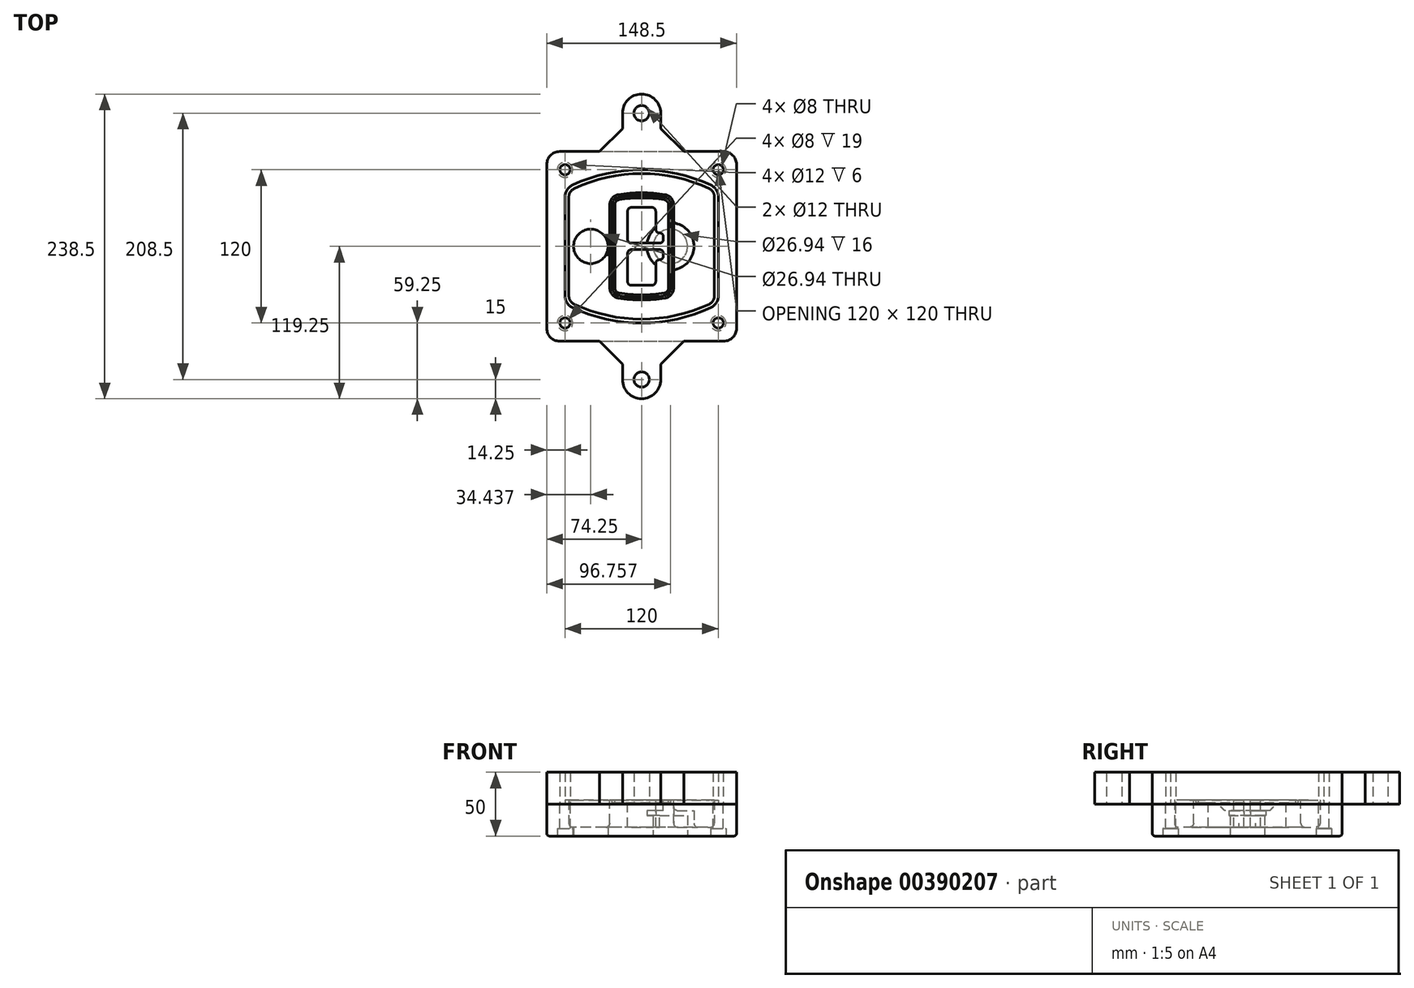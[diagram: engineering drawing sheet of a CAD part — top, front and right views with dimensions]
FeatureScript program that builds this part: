
annotation { "Feature Type Name" : "Feature", "Feature Type Description" : "" }
export const myFeature = defineFeature(function(context is Context, id is Id, definition is map)
    precondition{}
    {
        {
            var Q0;
            Q0=qCreatedBy(makeId("Top.planeOp"),FACE);
            var sketch = newSketch(context, id + "F0", { "sketchPlane" : qUnion([Q0])});
            skPoint(sketch, "E0.rect.middle", {"position": v(0, 0) * mm});
            skLineSegment(sketch, "E1.bottom", {"start": v(-64.25, -74.25) * mm, "end": v(64.25, -74.25) * mm});
            skLineSegment(sketch, "E1.top", {"start": v(-64.25, 74.25) * mm, "end": v(64.25, 74.25) * mm});
            skLineSegment(sketch, "E1.left", {"start": v(-74.25, -64.25) * mm, "end": v(-74.25, 64.25) * mm});
            skLineSegment(sketch, "E1.right", {"start": v(74.25, -64.25) * mm, "end": v(74.25, 64.25) * mm});
            skLineSegment(sketch, "E2", {"start": v(-74.25, 74.25) * mm, "end": v(74.25, -74.25) * mm, "construction": true});
            skLineSegment(sketch, "E3", {"start": v(74.25, 74.25) * mm, "end": v(-74.25, -74.25) * mm, "construction": true});
            skCircle(sketch, "E4", {"center": v(-60, 60) * mm, "radius": 4 * mm});
            skCircle(sketch, "E5", {"center": v(60, 60) * mm, "radius": 4 * mm});
            skCircle(sketch, "E6", {"center": v(60, -60) * mm, "radius": 4 * mm});
            skCircle(sketch, "E7", {"center": v(-60, -60) * mm, "radius": 4 * mm});
            skLineSegment(sketch, "E8", {"start": v(-60, 60) * mm, "end": v(60, 60) * mm, "construction": true});
            skLineSegment(sketch, "E9", {"start": v(60, 60) * mm, "end": v(60, -60) * mm, "construction": true});
            skLineSegment(sketch, "E10", {"start": v(60, -60) * mm, "end": v(-60, -60) * mm, "construction": true});
            skLineSegment(sketch, "E11", {"start": v(-60, -60) * mm, "end": v(-60, 60) * mm, "construction": true});
            skLineSegment(sketch, "E12", {"start": v(-60, 38.83) * mm, "end": v(-60, -38.83) * mm});
            skLineSegment(sketch, "E13", {"start": v(60, 38.83) * mm, "end": v(60, -38.83) * mm});
            skArc(sketch, "E14", {"start": v(54.26, 47.88) * mm, "mid": v(0, 60) * mm, "end": v(-54.26, 47.88) * mm});
            skArc(sketch, "E15", {"start": v(-54.26, -47.88) * mm, "mid": v(0, -60) * mm, "end": v(54.26, -47.88) * mm});
            skLineSegment(sketch, "E16", {"start": v(-60, 0) * mm, "end": v(60, 0) * mm, "construction": true});
            skPoint(sketch, "E17.visualSharp", {"position": v(-60, -45) * mm});
            skArc(sketch, "E17.filletArc", {"start": v(-60, -38.83) * mm, "mid": v(-58.44, -44.2) * mm, "end": v(-54.26, -47.88) * mm});
            skPoint(sketch, "E18.visualSharp", {"position": v(-60, 45) * mm});
            skArc(sketch, "E18.filletArc", {"start": v(-54.26, 47.88) * mm, "mid": v(-58.44, 44.2) * mm, "end": v(-60, 38.83) * mm});
            skPoint(sketch, "E19.visualSharp", {"position": v(60, 45) * mm});
            skArc(sketch, "E19.filletArc", {"start": v(60, 38.83) * mm, "mid": v(58.44, 44.2) * mm, "end": v(54.26, 47.88) * mm});
            skPoint(sketch, "E20.visualSharp", {"position": v(60, -45) * mm});
            skArc(sketch, "E20.filletArc", {"start": v(54.26, -47.88) * mm, "mid": v(58.44, -44.2) * mm, "end": v(60, -38.83) * mm});
            skPoint(sketch, "E21.visualSharp", {"position": v(-74.25, 74.25) * mm});
            skArc(sketch, "E21.filletArc", {"start": v(-64.25, 74.25) * mm, "mid": v(-71.32, 71.32) * mm, "end": v(-74.25, 64.25) * mm});
            skPoint(sketch, "E22.visualSharp", {"position": v(74.25, 74.25) * mm});
            skArc(sketch, "E22.filletArc", {"start": v(74.25, 64.25) * mm, "mid": v(71.32, 71.32) * mm, "end": v(64.25, 74.25) * mm});
            skPoint(sketch, "E23.visualSharp", {"position": v(74.25, -74.25) * mm});
            skArc(sketch, "E23.filletArc", {"start": v(64.25, -74.25) * mm, "mid": v(71.32, -71.32) * mm, "end": v(74.25, -64.25) * mm});
            skPoint(sketch, "E24.visualSharp", {"position": v(-74.25, -74.25) * mm});
            skArc(sketch, "E24.filletArc", {"start": v(-74.25, -64.25) * mm, "mid": v(-71.32, -71.32) * mm, "end": v(-64.25, -74.25) * mm});
            skArc(sketch, "E25.0", {"start": v(57, 38.83) * mm, "mid": v(55.9, 42.58) * mm, "end": v(52.98, 45.17) * mm});
            skLineSegment(sketch, "E25.1", {"start": v(57, 38.83) * mm, "end": v(57, -38.83) * mm});
            skArc(sketch, "E25.2", {"start": v(52.98, -45.17) * mm, "mid": v(55.9, -42.58) * mm, "end": v(57, -38.83) * mm});
            skArc(sketch, "E25.3", {"start": v(-52.98, -45.17) * mm, "mid": v(0, -57) * mm, "end": v(52.98, -45.17) * mm});
            skArc(sketch, "E25.4", {"start": v(-57, -38.83) * mm, "mid": v(-55.9, -42.58) * mm, "end": v(-52.98, -45.17) * mm});
            skArc(sketch, "E25.5", {"start": v(52.98, 45.17) * mm, "mid": v(0, 57) * mm, "end": v(-52.98, 45.17) * mm});
            skLineSegment(sketch, "E25.6", {"start": v(-57, 38.83) * mm, "end": v(-57, -38.83) * mm});
            skArc(sketch, "E25.7", {"start": v(-52.98, 45.17) * mm, "mid": v(-55.9, 42.58) * mm, "end": v(-57, 38.83) * mm});
            skArc(sketch, "E26.0", {"start": v(-55.96, 51.5) * mm, "mid": v(-61.82, 46.33) * mm, "end": v(-64, 38.83) * mm});
            skArc(sketch, "E26.1", {"start": v(55.96, 51.5) * mm, "mid": v(0, 64) * mm, "end": v(-55.96, 51.5) * mm});
            skArc(sketch, "E26.2", {"start": v(64, 38.83) * mm, "mid": v(61.82, 46.33) * mm, "end": v(55.96, 51.5) * mm});
            skLineSegment(sketch, "E26.3", {"start": v(64, 38.83) * mm, "end": v(64, -38.83) * mm});
            skArc(sketch, "E26.4", {"start": v(55.96, -51.5) * mm, "mid": v(61.82, -46.33) * mm, "end": v(64, -38.83) * mm});
            skLineSegment(sketch, "E26.5", {"start": v(-64, 38.83) * mm, "end": v(-64, -38.83) * mm});
            skArc(sketch, "E26.6", {"start": v(-55.96, -51.5) * mm, "mid": v(0, -64) * mm, "end": v(55.96, -51.5) * mm});
            skArc(sketch, "E26.7", {"start": v(-64, -38.83) * mm, "mid": v(-61.82, -46.33) * mm, "end": v(-55.96, -51.5) * mm});
            skSolve(sketch);
        }
        {
            var Q0;
            Q0=makeQuery(id+"F0.imprint","IMPRINT",FACE,{"disambiguationData":[TD([[makeQuery(id+"F0.imprint","IMPRINT",EDGE,{"derivedFrom":sQuery(id+"F0.wireOp",EDGE,"E1.bottom")}),1.0]])]});
            var Q1;
            Q1=makeQuery(id+"F0.imprint","IMPRINT",FACE,{"disambiguationData":[TD([[makeQuery(id+"F0.imprint","IMPRINT",EDGE,{"derivedFrom":sQuery(id+"F0.wireOp",EDGE,"E12")}),1.0]])]});
            var Q2;
            Q2=makeQuery(id+"F0.imprint","IMPRINT",FACE,{"disambiguationData":[TD([[makeQuery(id+"F0.imprint","IMPRINT",EDGE,{"derivedFrom":sQuery(id+"F0.wireOp",EDGE,"E25.0")}),1.0]])]});
            var Q3;
            Q3=makeQuery(id+"F0.imprint","IMPRINT",FACE,{"disambiguationData":[TD([[makeQuery(id+"F0.imprint","IMPRINT",EDGE,{"derivedFrom":sQuery(id+"F0.wireOp",EDGE,"E12")}),-1.0]])]});
            extrude(context, id + "F1", {"entities" : qUnion([Q0, Q1, Q2, Q3]), "oppositeDirection" : true, "depth" : 25 * mm});
        }
        {
            var Q0;
            Q0=makeQuery(id+"F0.imprint","IMPRINT",FACE,{"disambiguationData":[TD([[makeQuery(id+"F0.imprint","IMPRINT",EDGE,{"derivedFrom":sQuery(id+"F0.wireOp",EDGE,"E12")}),1.0]])]});
            extrude(context, id + "F2", {"entities" : qUnion([Q0]), "operationType" : NewBodyOperationType.ADD, "depth" : 3 * mm});
        }
        {
            var Q0;
            Q0=makeQuery(id+"F0.imprint","IMPRINT",FACE,{"disambiguationData":[TD([[makeQuery(id+"F0.imprint","IMPRINT",EDGE,{"derivedFrom":sQuery(id+"F0.wireOp",EDGE,"E25.0")}),1.0]])]});
            extrude(context, id + "F3", {"entities" : qUnion([Q0]), "operationType" : NewBodyOperationType.REMOVE, "oppositeDirection" : true, "depth" : 18 * mm});
        }
        {
            var Q0;
            Q0=makeQuery(id+"F2.opExtrude","CAP_FACE",FACE,{"disambiguationData":[OSD([sQuery(id+"F0.wireOp",EDGE,"E12"),sQuery(id+"F0.wireOp",EDGE,"E13"),sQuery(id+"F0.wireOp",EDGE,"E14"),sQuery(id+"F0.wireOp",EDGE,"E15"),sQuery(id+"F0.wireOp",EDGE,"E17.filletArc"),sQuery(id+"F0.wireOp",EDGE,"E18.filletArc"),sQuery(id+"F0.wireOp",EDGE,"E19.filletArc"),sQuery(id+"F0.wireOp",EDGE,"E20.filletArc"),sQuery(id+"F0.wireOp",EDGE,"E25.0"),sQuery(id+"F0.wireOp",EDGE,"E25.1"),sQuery(id+"F0.wireOp",EDGE,"E25.2"),sQuery(id+"F0.wireOp",EDGE,"E25.3"),sQuery(id+"F0.wireOp",EDGE,"E25.4"),sQuery(id+"F0.wireOp",EDGE,"E25.5"),sQuery(id+"F0.wireOp",EDGE,"E25.6"),sQuery(id+"F0.wireOp",EDGE,"E25.7")])],"isStart":false});
            var sketch = newSketch(context, id + "F4", { "sketchPlane" : qUnion([Q0])});
            skArc(sketch, "E27.0", {"start": v(-18.34, -40.45) * mm, "mid": v(0, -42) * mm, "end": v(18.34, -40.45) * mm});
            skArc(sketch, "E28.0", {"start": v(18.34, 40.45) * mm, "mid": v(0, 42) * mm, "end": v(-18.34, 40.45) * mm});
            skLineSegment(sketch, "E29", {"start": v(-25, 32.57) * mm, "end": v(-25, -32.57) * mm});
            skLineSegment(sketch, "E30", {"start": v(25, 32.57) * mm, "end": v(25, -32.57) * mm});
            skLineSegment(sketch, "E31", {"start": v(-25, 39.1) * mm, "end": v(25, 39.1) * mm, "construction": true});
            skLineSegment(sketch, "E32", {"start": v(-25, -39.1) * mm, "end": v(25, -39.1) * mm, "construction": true});
            skPoint(sketch, "E33.visualSharp", {"position": v(-25, 39.1) * mm});
            skArc(sketch, "E33.filletArc", {"start": v(-18.34, 40.45) * mm, "mid": v(-23.11, 37.73) * mm, "end": v(-25, 32.57) * mm});
            skPoint(sketch, "E34.visualSharp", {"position": v(25, 39.1) * mm});
            skArc(sketch, "E34.filletArc", {"start": v(25, 32.57) * mm, "mid": v(23.11, 37.73) * mm, "end": v(18.34, 40.45) * mm});
            skPoint(sketch, "E35.visualSharp", {"position": v(25, -39.1) * mm});
            skArc(sketch, "E35.filletArc", {"start": v(18.34, -40.45) * mm, "mid": v(23.11, -37.73) * mm, "end": v(25, -32.57) * mm});
            skPoint(sketch, "E36.visualSharp", {"position": v(-25, -39.1) * mm});
            skArc(sketch, "E36.filletArc", {"start": v(-25, -32.57) * mm, "mid": v(-23.11, -37.73) * mm, "end": v(-18.34, -40.45) * mm});
            skArc(sketch, "E37.0", {"start": v(52.98, 45.17) * mm, "mid": v(0, 57) * mm, "end": v(-52.98, 45.17) * mm});
            skArc(sketch, "E37.1", {"start": v(-52.98, 45.17) * mm, "mid": v(-55.9, 42.58) * mm, "end": v(-57, 38.83) * mm});
            skLineSegment(sketch, "E37.2", {"start": v(-57, 38.83) * mm, "end": v(-57, -38.83) * mm});
            skArc(sketch, "E37.3", {"start": v(-57, -38.83) * mm, "mid": v(-55.9, -42.58) * mm, "end": v(-52.98, -45.17) * mm});
            skArc(sketch, "E37.4", {"start": v(-52.98, -45.17) * mm, "mid": v(0, -57) * mm, "end": v(52.98, -45.17) * mm});
            skArc(sketch, "E37.5", {"start": v(52.98, -45.17) * mm, "mid": v(55.9, -42.58) * mm, "end": v(57, -38.83) * mm});
            skLineSegment(sketch, "E37.6", {"start": v(57, 38.83) * mm, "end": v(57, -38.83) * mm});
            skArc(sketch, "E37.7", {"start": v(57, 38.83) * mm, "mid": v(55.9, 42.58) * mm, "end": v(52.98, 45.17) * mm});
            skLineSegment(sketch, "E38.0", {"start": v(23, 32.57) * mm, "end": v(23, -32.57) * mm});
            skArc(sketch, "E38.1", {"start": v(18, -38.48) * mm, "mid": v(21.58, -36.44) * mm, "end": v(23, -32.57) * mm});
            skArc(sketch, "E38.2", {"start": v(-18, -38.48) * mm, "mid": v(0, -40) * mm, "end": v(18, -38.48) * mm});
            skArc(sketch, "E38.3", {"start": v(-23, -32.57) * mm, "mid": v(-21.58, -36.44) * mm, "end": v(-18, -38.48) * mm});
            skLineSegment(sketch, "E38.4", {"start": v(-23, 32.57) * mm, "end": v(-23, -32.57) * mm});
            skArc(sketch, "E38.5", {"start": v(23, 32.57) * mm, "mid": v(21.58, 36.44) * mm, "end": v(18, 38.48) * mm});
            skArc(sketch, "E38.6", {"start": v(-18, 38.48) * mm, "mid": v(-21.58, 36.44) * mm, "end": v(-23, 32.57) * mm});
            skArc(sketch, "E38.7", {"start": v(18, 38.48) * mm, "mid": v(0, 40) * mm, "end": v(-18, 38.48) * mm});
            skArc(sketch, "E39.0", {"start": v(21, 32.57) * mm, "mid": v(20.06, 35.15) * mm, "end": v(17.67, 36.5) * mm});
            skLineSegment(sketch, "E39.1", {"start": v(21, 32.57) * mm, "end": v(21, -32.57) * mm});
            skArc(sketch, "E39.2", {"start": v(17.67, -36.5) * mm, "mid": v(20.06, -35.15) * mm, "end": v(21, -32.57) * mm});
            skArc(sketch, "E39.3", {"start": v(-17.67, -36.5) * mm, "mid": v(0, -38) * mm, "end": v(17.67, -36.5) * mm});
            skArc(sketch, "E39.4", {"start": v(-21, -32.57) * mm, "mid": v(-20.06, -35.15) * mm, "end": v(-17.67, -36.5) * mm});
            skArc(sketch, "E39.5", {"start": v(17.67, 36.5) * mm, "mid": v(0, 38) * mm, "end": v(-17.67, 36.5) * mm});
            skLineSegment(sketch, "E39.6", {"start": v(-21, 32.57) * mm, "end": v(-21, -32.57) * mm});
            skArc(sketch, "E39.7", {"start": v(-17.67, 36.5) * mm, "mid": v(-20.06, 35.15) * mm, "end": v(-21, 32.57) * mm});
            skLineSegment(sketch, "E40", {"start": v(-25, 0) * mm, "end": v(25, 0) * mm, "construction": true});
            skLineSegment(sketch, "E41", {"start": v(-11, 5.5) * mm, "end": v(-11, 27.5) * mm});
            skLineSegment(sketch, "E42", {"start": v(-8, 30.5) * mm, "end": v(8, 30.5) * mm});
            skLineSegment(sketch, "E43", {"start": v(11, 27.5) * mm, "end": v(11, 13.5) * mm});
            skLineSegment(sketch, "E44", {"start": v(14, 10.5) * mm, "end": v(14, 10.5) * mm});
            skLineSegment(sketch, "E45", {"start": v(17, 7.5) * mm, "end": v(17, 5.5) * mm});
            skLineSegment(sketch, "E46", {"start": v(14, 2.5) * mm, "end": v(-8, 2.5) * mm});
            skPoint(sketch, "E47.visualSharp", {"position": v(-11, 30.5) * mm});
            skArc(sketch, "E47.filletArc", {"start": v(-8, 30.5) * mm, "mid": v(-10.12, 29.62) * mm, "end": v(-11, 27.5) * mm});
            skPoint(sketch, "E48.visualSharp", {"position": v(11, 30.5) * mm});
            skArc(sketch, "E48.filletArc", {"start": v(11, 27.5) * mm, "mid": v(10.12, 29.62) * mm, "end": v(8, 30.5) * mm});
            skPoint(sketch, "E49.visualSharp", {"position": v(11, 10.5) * mm});
            skArc(sketch, "E49.filletArc", {"start": v(11, 13.5) * mm, "mid": v(11.88, 11.38) * mm, "end": v(14, 10.5) * mm});
            skPoint(sketch, "E50.visualSharp", {"position": v(17, 10.5) * mm});
            skArc(sketch, "E50.filletArc", {"start": v(17, 7.5) * mm, "mid": v(16.12, 9.62) * mm, "end": v(14, 10.5) * mm});
            skPoint(sketch, "E51.visualSharp", {"position": v(17, 2.5) * mm});
            skArc(sketch, "E51.filletArc", {"start": v(14, 2.5) * mm, "mid": v(16.12, 3.38) * mm, "end": v(17, 5.5) * mm});
            skPoint(sketch, "E52.visualSharp", {"position": v(-11, 2.5) * mm});
            skArc(sketch, "E52.filletArc", {"start": v(-11, 5.5) * mm, "mid": v(-10.12, 3.38) * mm, "end": v(-8, 2.5) * mm});
            skLineSegment(sketch, "E53.0.MirrorCS", {"start": v(14, -2.5) * mm, "end": v(-8, -2.5) * mm});
            skArc(sketch, "E54.0.MirrorCS", {"start": v(-11, -5.5) * mm, "mid": v(-10.12, -3.38) * mm, "end": v(-8, -2.5) * mm});
            skLineSegment(sketch, "E55.0.MirrorCS", {"start": v(-11, -5.5) * mm, "end": v(-11, -27.5) * mm});
            skArc(sketch, "E56.0.MirrorCS", {"start": v(-8, -30.5) * mm, "mid": v(-10.12, -29.62) * mm, "end": v(-11, -27.5) * mm});
            skLineSegment(sketch, "E57.0.MirrorCS", {"start": v(-8, -30.5) * mm, "end": v(8, -30.5) * mm});
            skArc(sketch, "E58.0.MirrorCS", {"start": v(11, -27.5) * mm, "mid": v(10.12, -29.62) * mm, "end": v(8, -30.5) * mm});
            skLineSegment(sketch, "E59.0.MirrorCS", {"start": v(11, -27.5) * mm, "end": v(11, -13.5) * mm});
            skArc(sketch, "E60.0.MirrorCS", {"start": v(11, -13.5) * mm, "mid": v(11.88, -11.38) * mm, "end": v(14, -10.5) * mm});
            skArc(sketch, "E61.0.MirrorCS", {"start": v(17, -7.5) * mm, "mid": v(16.12, -9.62) * mm, "end": v(14, -10.5) * mm});
            skLineSegment(sketch, "E62.0.MirrorCS", {"start": v(17, -7.5) * mm, "end": v(17, -5.5) * mm});
            skArc(sketch, "E63.0.MirrorCS", {"start": v(14, -2.5) * mm, "mid": v(16.12, -3.38) * mm, "end": v(17, -5.5) * mm});
            skSolve(sketch);
        }
        {
            var Q0;
            Q0=makeQuery(id+"F4.imprint","IMPRINT",FACE,{"disambiguationData":[TD([[makeQuery(id+"F4.imprint","IMPRINT",EDGE,{"derivedFrom":sQuery(id+"F4.wireOp",EDGE,"E27.0")}),1.0]])]});
            var Q1;
            Q1=makeQuery(id+"F4.imprint","IMPRINT",FACE,{"disambiguationData":[TD([[makeQuery(id+"F4.imprint","IMPRINT",EDGE,{"derivedFrom":sQuery(id+"F4.wireOp",EDGE,"E38.0")}),-1.0]])]});
            var Q2;
            Q2=makeQuery(id+"F4.imprint","IMPRINT",FACE,{"disambiguationData":[TD([[makeQuery(id+"F4.imprint","IMPRINT",EDGE,{"derivedFrom":sQuery(id+"F4.wireOp",EDGE,"E39.0")}),1.0]])]});
            extrude(context, id + "F5", {"entities" : qUnion([Q0, Q1, Q2]), "operationType" : NewBodyOperationType.ADD, "endBound" : BoundingType.UP_TO_NEXT, "oppositeDirection" : true, "depth" : 25 * mm});
        }
        {
            var Q0;
            Q0=makeQuery(id+"F4.imprint","IMPRINT",FACE,{"disambiguationData":[TD([[makeQuery(id+"F4.imprint","IMPRINT",EDGE,{"derivedFrom":sQuery(id+"F4.wireOp",EDGE,"E38.0")}),-1.0]])]});
            extrude(context, id + "F6", {"entities" : qUnion([Q0]), "operationType" : NewBodyOperationType.REMOVE, "oppositeDirection" : true, "depth" : 2 * mm});
        }
        {
            var Q0;
            Q0=makeQuery(id+"F1.opExtrude","CAP_FACE",FACE,{"disambiguationData":[OSD([sQuery(id+"F0.wireOp",EDGE,"E1.bottom"),sQuery(id+"F0.wireOp",EDGE,"E1.top"),sQuery(id+"F0.wireOp",EDGE,"E1.left"),sQuery(id+"F0.wireOp",EDGE,"E1.right"),sQuery(id+"F0.wireOp",EDGE,"E4"),sQuery(id+"F0.wireOp",EDGE,"E5"),sQuery(id+"F0.wireOp",EDGE,"E6"),sQuery(id+"F0.wireOp",EDGE,"E7"),sQuery(id+"F0.wireOp",EDGE,"E21.filletArc"),sQuery(id+"F0.wireOp",EDGE,"E22.filletArc"),sQuery(id+"F0.wireOp",EDGE,"E23.filletArc"),sQuery(id+"F0.wireOp",EDGE,"E24.filletArc")])],"isStart":false});
            var sketch = newSketch(context, id + "F7", { "sketchPlane" : qUnion([Q0])});
            skCircle(sketch, "E64", {"center": v(22.5, 0) * mm, "radius": 13.47 * mm});
            skCircle(sketch, "E65", {"center": v(-39.81, 0) * mm, "radius": 13.47 * mm});
            skLineSegment(sketch, "E66", {"start": v(74.25, 0) * mm, "end": v(-74.25, 0) * mm});
            skCircle(sketch, "E67", {"center": v(22.5, 0) * mm, "radius": 18.47 * mm});
            skCircle(sketch, "E68", {"center": v(60, -60) * mm, "radius": 6 * mm});
            skCircle(sketch, "E69", {"center": v(-60, -60) * mm, "radius": 6 * mm});
            skCircle(sketch, "E70", {"center": v(-60, 60) * mm, "radius": 6 * mm});
            skCircle(sketch, "E71", {"center": v(60, 60) * mm, "radius": 6 * mm});
            skSolve(sketch);
        }
        {
            var Q0;
            {var subQ1=sQuery(id+"F7.wireOp",EDGE,"E66");var subQ4=sQuery(id+"F7.wireOp",EDGE,"E64");var subQ6=makeQuery(id+"F7.imprint","INTERSECT",VERTEX,{"disambiguationData":[OD(0.0)],"derivedFrom":[subQ4,subQ1]});Q0=makeQuery(id+"F7.imprint","IMPRINT",FACE,{"disambiguationData":[TD([[makeQuery(id+"F7.imprint","IMPRINT",EDGE,{"disambiguationData":[TD([[subQ6,-1.0]])],"derivedFrom":subQ4}),-1.0]])]});}
            var Q1;
            {var subQ0=sQuery(id+"F7.wireOp",EDGE,"E66");var subQ1=sQuery(id+"F7.wireOp",EDGE,"E64");var subQ3=makeQuery(id+"F7.imprint","INTERSECT",VERTEX,{"disambiguationData":[OD(0.0)],"derivedFrom":[subQ1,subQ0]});Q1=makeQuery(id+"F7.imprint","IMPRINT",FACE,{"disambiguationData":[TD([[makeQuery(id+"F7.imprint","IMPRINT",EDGE,{"disambiguationData":[TD([[subQ3,-1.0]])],"derivedFrom":subQ1}),1.0]])]});}
            var Q2;
            {var subQ0=sQuery(id+"F7.wireOp",EDGE,"E66");var subQ1=sQuery(id+"F7.wireOp",EDGE,"E64");var subQ3=makeQuery(id+"F7.imprint","INTERSECT",VERTEX,{"disambiguationData":[OD(0.0)],"derivedFrom":[subQ1,subQ0]});Q2=makeQuery(id+"F7.imprint","IMPRINT",FACE,{"disambiguationData":[TD([[makeQuery(id+"F7.imprint","IMPRINT",EDGE,{"disambiguationData":[TD([[subQ3,1.0]])],"derivedFrom":subQ1}),1.0]])]});}
            var Q3;
            {var subQ1=sQuery(id+"F7.wireOp",EDGE,"E66");var subQ4=sQuery(id+"F7.wireOp",EDGE,"E64");var subQ6=makeQuery(id+"F7.imprint","INTERSECT",VERTEX,{"disambiguationData":[OD(0.0)],"derivedFrom":[subQ4,subQ1]});Q3=makeQuery(id+"F7.imprint","IMPRINT",FACE,{"disambiguationData":[TD([[makeQuery(id+"F7.imprint","IMPRINT",EDGE,{"disambiguationData":[TD([[subQ6,1.0]])],"derivedFrom":subQ4}),-1.0]])]});}
            extrude(context, id + "F8", {"entities" : qUnion([Q0, Q1, Q2, Q3]), "operationType" : NewBodyOperationType.ADD, "oppositeDirection" : true, "depth" : 20 * mm});
        }
        {
            var Q0;
            {var subQ0=sQuery(id+"F7.wireOp",EDGE,"E66");var subQ1=sQuery(id+"F7.wireOp",EDGE,"E64");var subQ3=makeQuery(id+"F7.imprint","INTERSECT",VERTEX,{"disambiguationData":[OD(0.0)],"derivedFrom":[subQ1,subQ0]});Q0=makeQuery(id+"F7.imprint","IMPRINT",FACE,{"disambiguationData":[TD([[makeQuery(id+"F7.imprint","IMPRINT",EDGE,{"disambiguationData":[TD([[subQ3,-1.0]])],"derivedFrom":subQ1}),1.0]])]});}
            var Q1;
            {var subQ0=sQuery(id+"F7.wireOp",EDGE,"E66");var subQ1=sQuery(id+"F7.wireOp",EDGE,"E64");var subQ3=makeQuery(id+"F7.imprint","INTERSECT",VERTEX,{"disambiguationData":[OD(0.0)],"derivedFrom":[subQ1,subQ0]});Q1=makeQuery(id+"F7.imprint","IMPRINT",FACE,{"disambiguationData":[TD([[makeQuery(id+"F7.imprint","IMPRINT",EDGE,{"disambiguationData":[TD([[subQ3,1.0]])],"derivedFrom":subQ1}),1.0]])]});}
            extrude(context, id + "F9", {"entities" : qUnion([Q0, Q1]), "operationType" : NewBodyOperationType.REMOVE, "oppositeDirection" : true, "depth" : 16 * mm});
        }
        {
            var Q0;
            {var subQ0=sQuery(id+"F7.wireOp",EDGE,"E66");var subQ1=sQuery(id+"F7.wireOp",EDGE,"E65");var subQ3=makeQuery(id+"F7.imprint","INTERSECT",VERTEX,{"disambiguationData":[OD(0.0)],"derivedFrom":[subQ1,subQ0]});Q0=makeQuery(id+"F7.imprint","IMPRINT",FACE,{"disambiguationData":[TD([[makeQuery(id+"F7.imprint","IMPRINT",EDGE,{"disambiguationData":[TD([[subQ3,-1.0]])],"derivedFrom":subQ1}),1.0]])]});}
            var Q1;
            {var subQ0=sQuery(id+"F7.wireOp",EDGE,"E66");var subQ1=sQuery(id+"F7.wireOp",EDGE,"E65");var subQ3=makeQuery(id+"F7.imprint","INTERSECT",VERTEX,{"disambiguationData":[OD(0.0)],"derivedFrom":[subQ1,subQ0]});Q1=makeQuery(id+"F7.imprint","IMPRINT",FACE,{"disambiguationData":[TD([[makeQuery(id+"F7.imprint","IMPRINT",EDGE,{"disambiguationData":[TD([[subQ3,1.0]])],"derivedFrom":subQ1}),1.0]])]});}
            extrude(context, id + "F10", {"entities" : qUnion([Q0, Q1]), "operationType" : NewBodyOperationType.REMOVE, "oppositeDirection" : true, "depth" : 25 * mm});
        }
        {
            var Q0;
            Q0=makeQuery(id+"F7.imprint","IMPRINT",FACE,{"disambiguationData":[TD([[makeQuery(id+"F7.imprint","IMPRINT",EDGE,{"derivedFrom":sQuery(id+"F7.wireOp",EDGE,"E68")}),1.0]])]});
            var Q1;
            Q1=makeQuery(id+"F7.imprint","IMPRINT",FACE,{"disambiguationData":[TD([[makeQuery(id+"F7.imprint","IMPRINT",EDGE,{"derivedFrom":makeQuery(id+"F1.opExtrude","CAP_EDGE",EDGE,{"disambiguationData":[OSD([sQuery(id+"F0.wireOp",EDGE,"E5")])],"isStart":false})}),-1.0]])]});
            var Q2;
            Q2=makeQuery(id+"F7.imprint","IMPRINT",FACE,{"disambiguationData":[TD([[makeQuery(id+"F7.imprint","IMPRINT",EDGE,{"derivedFrom":sQuery(id+"F7.wireOp",EDGE,"E69")}),1.0]])]});
            var Q3;
            Q3=makeQuery(id+"F7.imprint","IMPRINT",FACE,{"disambiguationData":[TD([[makeQuery(id+"F7.imprint","IMPRINT",EDGE,{"derivedFrom":makeQuery(id+"F1.opExtrude","CAP_EDGE",EDGE,{"disambiguationData":[OSD([sQuery(id+"F0.wireOp",EDGE,"E4")])],"isStart":false})}),-1.0]])]});
            var Q4;
            Q4=makeQuery(id+"F7.imprint","IMPRINT",FACE,{"disambiguationData":[TD([[makeQuery(id+"F7.imprint","IMPRINT",EDGE,{"derivedFrom":sQuery(id+"F7.wireOp",EDGE,"E70")}),1.0]])]});
            var Q5;
            Q5=makeQuery(id+"F7.imprint","IMPRINT",FACE,{"disambiguationData":[TD([[makeQuery(id+"F7.imprint","IMPRINT",EDGE,{"derivedFrom":makeQuery(id+"F1.opExtrude","CAP_EDGE",EDGE,{"disambiguationData":[OSD([sQuery(id+"F0.wireOp",EDGE,"E7")])],"isStart":false})}),-1.0]])]});
            var Q6;
            Q6=makeQuery(id+"F7.imprint","IMPRINT",FACE,{"disambiguationData":[TD([[makeQuery(id+"F7.imprint","IMPRINT",EDGE,{"derivedFrom":sQuery(id+"F7.wireOp",EDGE,"E71")}),1.0]])]});
            var Q7;
            Q7=makeQuery(id+"F7.imprint","IMPRINT",FACE,{"disambiguationData":[TD([[makeQuery(id+"F7.imprint","IMPRINT",EDGE,{"derivedFrom":makeQuery(id+"F1.opExtrude","CAP_EDGE",EDGE,{"disambiguationData":[OSD([sQuery(id+"F0.wireOp",EDGE,"E6")])],"isStart":false})}),-1.0]])]});
            extrude(context, id + "F11", {"entities" : qUnion([Q0, Q1, Q2, Q3, Q4, Q5, Q6, Q7]), "operationType" : NewBodyOperationType.REMOVE, "oppositeDirection" : true, "depth" : 6 * mm});
        }
        {
            var Q0;
            Q0=makeQuery(id+"F9.boolean.opBoolean","COPY",FACE,{"derivedFrom":makeQuery(id+"F9.opExtrude","CAP_FACE",FACE,{"disambiguationData":[OSD([sQuery(id+"F7.wireOp",EDGE,"E64")])],"isStart":false})});
            var sketch = newSketch(context, id + "F12", { "sketchPlane" : qUnion([Q0])});
            skArc(sketch, "E72.0", {"start": v(11, 14.45) * mm, "mid": v(6.45, 9.13) * mm, "end": v(4.2, 2.5) * mm});
            skArc(sketch, "E72.1", {"start": v(4.2, -2.5) * mm, "mid": v(6.45, -9.13) * mm, "end": v(11, -14.45) * mm});
            skLineSegment(sketch, "E73", {"start": v(4.2, -2.5) * mm, "end": v(14, -2.5) * mm});
            skLineSegment(sketch, "E74.0", {"start": v(14, 2.5) * mm, "end": v(4.2, 2.5) * mm});
            skArc(sketch, "E74.1", {"start": v(14, 2.5) * mm, "mid": v(16.12, 3.38) * mm, "end": v(17, 5.5) * mm});
            skLineSegment(sketch, "E74.2", {"start": v(17, 7.5) * mm, "end": v(17, 5.5) * mm});
            skArc(sketch, "E74.3", {"start": v(17, 7.5) * mm, "mid": v(16.12, 9.62) * mm, "end": v(14, 10.5) * mm});
            skArc(sketch, "E74.4", {"start": v(11, 13.5) * mm, "mid": v(11.88, 11.38) * mm, "end": v(14, 10.5) * mm});
            skLineSegment(sketch, "E74.5", {"start": v(11, 14.45) * mm, "end": v(11, 13.5) * mm});
            skLineSegment(sketch, "E74.7", {"start": v(14, -2.5) * mm, "end": v(4.2, -2.5) * mm});
            skArc(sketch, "E74.8", {"start": v(14, -2.5) * mm, "mid": v(16.12, -3.38) * mm, "end": v(17, -5.5) * mm});
            skLineSegment(sketch, "E74.9", {"start": v(17, -7.5) * mm, "end": v(17, -5.5) * mm});
            skArc(sketch, "E74.10", {"start": v(17, -7.5) * mm, "mid": v(16.12, -9.62) * mm, "end": v(14, -10.5) * mm});
            skArc(sketch, "E74.11", {"start": v(11, -13.5) * mm, "mid": v(11.88, -11.38) * mm, "end": v(14, -10.5) * mm});
            skLineSegment(sketch, "E74.12", {"start": v(11, -14.45) * mm, "end": v(11, -13.5) * mm});
            skPoint(sketch, "E75.orphan", {"position": v(11, -27.5) * mm});
            skPoint(sketch, "E76.orphan", {"position": v(-8, -2.5) * mm});
            skPoint(sketch, "E77.orphan", {"position": v(-8, 2.5) * mm});
            skPoint(sketch, "E78.orphan", {"position": v(11, 27.5) * mm});
            skSolve(sketch);
        }
        {
            var Q0;
            {var subQ7=sQuery(id+"F12.wireOp",EDGE,"E72.0");var subQ14=sQuery(id+"F12.wireOp",EDGE,"E72.1");var subQ16=sQuery(id+"F12.wireOp",EDGE,"E74.1");var subQ18=sQuery(id+"F12.wireOp",EDGE,"E74.8");Q0=qUnion([makeQuery(id+"F12.imprint","IMPRINT",FACE,{"disambiguationData":[TD([[makeQuery(id+"F12.imprint","IMPRINT",EDGE,{"derivedFrom":subQ7}),1.0]])]}),makeQuery(id+"F12.imprint","IMPRINT",FACE,{"disambiguationData":[TD([[makeQuery(id+"F12.imprint","IMPRINT",EDGE,{"derivedFrom":subQ14}),1.0]])]}),makeQuery(id+"F12.imprint","IMPRINT",FACE,{"disambiguationData":[TD([[makeQuery(id+"F12.imprint","IMPRINT",EDGE,{"derivedFrom":subQ16}),1.0]])]}),makeQuery(id+"F12.imprint","IMPRINT",FACE,{"disambiguationData":[TD([[makeQuery(id+"F12.imprint","IMPRINT",EDGE,{"derivedFrom":subQ18}),-1.0]])]})]);}
            var Q1;
            Q1=makeQuery(id+"F5.boolean.opBoolean","SPLIT",FACE,{"disambiguationData":[TD([makeQuery(id+"F5.opExtrude","SWEPT_FACE",FACE,{"disambiguationData":[OSD([sQuery(id+"F4.wireOp",EDGE,"E41")])]})])],"derivedFrom":makeQuery(id+"F3.boolean.opBoolean","COPY",FACE,{"derivedFrom":makeQuery(id+"F3.opExtrude","CAP_FACE",FACE,{"disambiguationData":[OSD([sQuery(id+"F0.wireOp",EDGE,"E25.0"),sQuery(id+"F0.wireOp",EDGE,"E25.1"),sQuery(id+"F0.wireOp",EDGE,"E25.2"),sQuery(id+"F0.wireOp",EDGE,"E25.3"),sQuery(id+"F0.wireOp",EDGE,"E25.4"),sQuery(id+"F0.wireOp",EDGE,"E25.5"),sQuery(id+"F0.wireOp",EDGE,"E25.6"),sQuery(id+"F0.wireOp",EDGE,"E25.7")])],"isStart":false})})});
            extrude(context, id + "F13", {"entities" : qUnion([Q0]), "operationType" : NewBodyOperationType.REMOVE, "endBound" : BoundingType.UP_TO_SURFACE, "endBoundEntityFace" : qUnion([Q1]), "depth" : 25 * mm});
        }
        {
            var Q0;
            Q0=makeQuery(id+"F3.boolean.opBoolean","COPY",EDGE,{"derivedFrom":makeQuery(id+"F3.opExtrude","CAP_EDGE",EDGE,{"disambiguationData":[OSD([sQuery(id+"F0.wireOp",EDGE,"E25.6")])],"isStart":false})});
            var Q1;
            Q1=makeQuery(id+"F8.boolean.opBoolean","INTERSECT",EDGE,{"derivedFrom":[makeQuery(id+"F5.opExtrude","SWEPT_FACE",FACE,{"disambiguationData":[OSD([sQuery(id+"F4.wireOp",EDGE,"E30")])]}),makeQuery(id+"F8.opExtrude","CAP_FACE",FACE,{"disambiguationData":[OSD([sQuery(id+"F7.wireOp",EDGE,"E67")])],"isStart":false})]});
            var Q2;
            Q2=makeQuery(id+"F8.boolean.opBoolean","INTERSECT",EDGE,{"disambiguationData":[OD(1.0)],"derivedFrom":[makeQuery(id+"F5.opExtrude","SWEPT_FACE",FACE,{"disambiguationData":[OSD([sQuery(id+"F4.wireOp",EDGE,"E30")])]}),makeQuery(id+"F8.opExtrude","SWEPT_FACE",FACE,{"disambiguationData":[OSD([sQuery(id+"F7.wireOp",EDGE,"E67")])]})]});
            var Q3;
            {var subQ0=sQuery(id+"F4.wireOp",EDGE,"E30");Q3=makeQuery(id+"F8.boolean.opBoolean","SPLIT",EDGE,{"disambiguationData":[TD([makeQuery(id+"F5.opExtrude","SWEPT_FACE",FACE,{"disambiguationData":[OSD([sQuery(id+"F4.wireOp",EDGE,"E35.filletArc")])]})])],"derivedFrom":makeQuery(id+"F5.opExtrude","CAP_EDGE",EDGE,{"disambiguationData":[OSD([subQ0])],"isStart":false})});}
            var Q4;
            {var subQ0=sQuery(id+"F0.wireOp",EDGE,"E25.7");var subQ1=sQuery(id+"F0.wireOp",EDGE,"E25.1");var subQ2=sQuery(id+"F0.wireOp",EDGE,"E25.6");var subQ3=sQuery(id+"F0.wireOp",EDGE,"E25.5");var subQ4=sQuery(id+"F0.wireOp",EDGE,"E25.4");var subQ5=sQuery(id+"F0.wireOp",EDGE,"E25.0");var subQ6=sQuery(id+"F0.wireOp",EDGE,"E25.2");var subQ7=sQuery(id+"F0.wireOp",EDGE,"E25.3");Q4=makeQuery(id+"F8.boolean.opBoolean","INTERSECT",EDGE,{"derivedFrom":[makeQuery(id+"F5.boolean.opBoolean","SPLIT",FACE,{"disambiguationData":[TD([makeQuery(id+"F2.opExtrude","SWEPT_FACE",FACE,{"disambiguationData":[OSD([subQ5])]})])],"derivedFrom":makeQuery(id+"F3.boolean.opBoolean","COPY",FACE,{"derivedFrom":makeQuery(id+"F3.opExtrude","CAP_FACE",FACE,{"disambiguationData":[OSD([subQ5,subQ1,subQ6,subQ7,subQ4,subQ3,subQ2,subQ0])],"isStart":false})})}),makeQuery(id+"F8.opExtrude","SWEPT_FACE",FACE,{"disambiguationData":[OSD([sQuery(id+"F7.wireOp",EDGE,"E67")])]})]});}
            var Q5;
            Q5=makeQuery(id+"F8.boolean.opBoolean","INTERSECT",EDGE,{"disambiguationData":[OD(0.0)],"derivedFrom":[makeQuery(id+"F5.opExtrude","SWEPT_FACE",FACE,{"disambiguationData":[OSD([sQuery(id+"F4.wireOp",EDGE,"E30")])]}),makeQuery(id+"F8.opExtrude","SWEPT_FACE",FACE,{"disambiguationData":[OSD([sQuery(id+"F7.wireOp",EDGE,"E67")])]})]});
            fillet(context, id + "F14", {"entities" : qUnion([Q0, Q1, Q2, Q3, Q4, Q5]), "radius" : 3 * mm, "tangentPropagation" : true, "allowEdgeOverflow" : false});
        }
        {
            var Q0;
            Q0=makeQuery(id+"F1.opExtrude","CAP_EDGE",EDGE,{"disambiguationData":[OSD([sQuery(id+"F0.wireOp",EDGE,"E1.bottom")])],"isStart":false});
            fillet(context, id + "F15", {"entities" : qUnion([Q0]), "radius" : 2 * mm, "tangentPropagation" : true, "allowEdgeOverflow" : false});
        }
        {
            var Q0;
            {var subQ0=sQuery(id+"F0.wireOp",EDGE,"E21.filletArc");var subQ1=sQuery(id+"F0.wireOp",EDGE,"E7");var subQ2=sQuery(id+"F0.wireOp",EDGE,"E6");var subQ3=sQuery(id+"F0.wireOp",EDGE,"E5");var subQ4=sQuery(id+"F0.wireOp",EDGE,"E4");var subQ5=sQuery(id+"F0.wireOp",EDGE,"E22.filletArc");var subQ6=sQuery(id+"F0.wireOp",EDGE,"E1.bottom");var subQ7=sQuery(id+"F0.wireOp",EDGE,"E1.right");var subQ8=sQuery(id+"F0.wireOp",EDGE,"E1.top");var subQ9=sQuery(id+"F0.wireOp",EDGE,"E1.left");var subQ10=sQuery(id+"F0.wireOp",EDGE,"E23.filletArc");var subQ11=sQuery(id+"F0.wireOp",EDGE,"E24.filletArc");Q0=makeQuery(id+"F2.boolean.opBoolean","SPLIT",FACE,{"disambiguationData":[TD([makeQuery(id+"F1.opExtrude","SWEPT_FACE",FACE,{"disambiguationData":[OSD([subQ6])]})])],"derivedFrom":makeQuery(id+"F1.opExtrude","CAP_FACE",FACE,{"disambiguationData":[OSD([subQ6,subQ8,subQ9,subQ7,subQ4,subQ3,subQ2,subQ1,subQ0,subQ5,subQ10,subQ11])],"isStart":true})});}
            var sketch = newSketch(context, id + "F16", { "sketchPlane" : qUnion([Q0])});
            skCircle(sketch, "E79", {"center": v(0, 104.25) * mm, "radius": 6 * mm});
            skPoint(sketch, "E79.centerSnap0", {"position": v(0, 74.25) * mm});
            skLineSegment(sketch, "E80", {"start": v(-15, 104.25) * mm, "end": v(-15, 92.25) * mm});
            skArc(sketch, "E81", {"start": v(15, 104.25) * mm, "mid": v(0, 119.25) * mm, "end": v(-15, 104.25) * mm});
            skLineSegment(sketch, "E82", {"start": v(15, 104.25) * mm, "end": v(15, 92.25) * mm});
            skLineSegment(sketch, "E83", {"start": v(-15, 92.25) * mm, "end": v(-33, 74.25) * mm});
            skLineSegment(sketch, "E84", {"start": v(15, 92.25) * mm, "end": v(33, 74.25) * mm});
            skLineSegment(sketch, "E85.MirrorCS", {"start": v(-3, 92.25) * mm, "end": v(-15, 92.25) * mm});
            skLineSegment(sketch, "E86.MirrorCS", {"start": v(-15, -92.25) * mm, "end": v(-33, -74.25) * mm});
            skLineSegment(sketch, "E87.MirrorCS", {"start": v(-15, -104.25) * mm, "end": v(-15, -92.25) * mm});
            skArc(sketch, "E88.MirrorCS", {"start": v(15, -104.25) * mm, "mid": v(0, -119.25) * mm, "end": v(-15, -104.25) * mm});
            skLineSegment(sketch, "E89.MirrorCS", {"start": v(15, -104.25) * mm, "end": v(15, -92.25) * mm});
            skLineSegment(sketch, "E90.MirrorCS", {"start": v(15, -92.25) * mm, "end": v(33, -74.25) * mm});
            skCircle(sketch, "E91.MirrorC", {"center": v(0, -104.25) * mm, "radius": 6 * mm});
            skSolve(sketch);
        }
        {
            var Q0;
            Q0=makeQuery(id+"F16.imprint","IMPRINT",FACE,{"disambiguationData":[TD([[makeQuery(id+"F16.imprint","IMPRINT",EDGE,{"derivedFrom":makeQuery(id+"F1.opExtrude","CAP_EDGE",EDGE,{"disambiguationData":[OSD([sQuery(id+"F0.wireOp",EDGE,"E1.left")])],"isStart":true})}),-1.0]])]});
            var Q1;
            {var subQ0=sQuery(id+"F16.wireOp",EDGE,"E86.MirrorCS");Q1=makeQuery(id+"F16.imprint","IMPRINT",FACE,{"disambiguationData":[TD([[makeQuery(id+"F16.imprint","IMPRINT",EDGE,{"derivedFrom":subQ0}),-1.0]])]});}
            var Q2;
            Q2=makeQuery(id+"F16.imprint","IMPRINT",FACE,{"disambiguationData":[TD([[makeQuery(id+"F16.imprint","IMPRINT",EDGE,{"derivedFrom":sQuery(id+"F16.wireOp",EDGE,"E79")}),-1.0]])]});
            extrude(context, id + "F17", {"entities" : qUnion([Q0, Q1, Q2]), "depth" : 25 * mm});
        }
    });
